# Revit family: Table-Teknion-Zones_ZNTBS-R2015
name_source: partatom
category: Furniture
revit_build: Autodesk Revit Architecture 2015 (Build: 20140322_1515(x64)
units: mm (PartAtom-declared; Revit-internal decimal feet)

## types (3) — shared parameters
Assembly Code = E2020200
Depth = 36"
Manufacturer = Teknion
Manufacturer Fax = 416.661.4586
Part Number = ZNTBS
Product Documentation Link = http://www.teknion.com
Product Line = Zones
Product Page URL = http://www.teknion.com
Series = Zones
Sustainability Data = http://www.teknion.com
URL = http://www.teknion.com
Warranty = http://www.teknion.com
Width = 36"

## per-type parameters (varying)
| type | Description | Height | Model |
| Task Height | Soft Square Bistro Table, Task Height, 36"dia | 29" | ZNTBST36 |
| Counter Height | Soft Square Bistro Table, Counter Height, 36"d | 36" | ZNTBSC36 |
| Bar Height | Soft Square Bistro Table, Bar Height, 36"d | 42" | ZNTBSB36 |

## geometry (parser evidence)
native form markers: Blend x10, Sweep x5
no freeform markers — native parametric forms only
